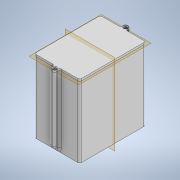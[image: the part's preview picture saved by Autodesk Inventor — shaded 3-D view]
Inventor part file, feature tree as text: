
AUTODESK INVENTOR PART (.ipt)
format: ipt  version: 2020 (Build 240168000, 168)  size: 301,056 bytes
history: native  units: mm
features: sketch x5, extrude x4, plane x2, fillet x2, shell x1, hole x1, chamfer x1, split x1
ambient origin geometry x8: Origin, YZ Plane, XZ Plane, XY Plane, X Axis, Y Axis, Z Axis, Center Point
bodies: Solid1 (feature_tree), Solid4 (feature_tree), Solid5 (feature_tree)
feature tree (17):
  extrude  "Extrusion1"  Depth=42.0mm
  shell  "Shell1"  Thickness=70.0mm
  plane  "Work Plane1"
  extrude  "Extrusion2"  [1 undecoded]
  extrude  "Extrusion3"  Depth=5.0mm
  hole  "Hole1"  [1 undecoded]
  chamfer  "Chamfer1"  Distance=5.0mm
  fillet  "Fillet2"  Radius=2.0mm
  split  "Split2"
  fillet  "Fillet3"  Radius=4.0mm
  plane  "Work Plane2"
  extrude  "Extrusion5"  Depth=2.0mm
  sketch  "Sketch1"  dims[d0=63.0mm d1=42.0mm d2=70.0mm d3=0.0mm]
  sketch  "Sketch3"  dims[d4=2.0mm d5=-2.0mm]
  sketch  "Sketch4"  dims[d9=74.0mm d10=5.0mm]
  sketch  "Sketch6"  dims[d11=5.0mm d12=0.0mm d13=5.0mm d14=5.0mm d15=0.0mm]
  sketch  "Sketch8"  dims[d16=3.242mm d17=8.0mm d18=4.5mm d19=3.4mm d20=90.0deg d21=11.8mm d22=20.594885mm d23=5.0mm d24=2.0mm d25=45.0deg d27=4.0mm d31=2.0mm d32=4.0mm d33=10.0mm d34=10.0mm d35=7.0mm d36=2.0mm d39=3.0mm d40=2.0mm d41=2.0mm d42=2.0mm d43=2.0mm d44=2.0mm d45=20.0mm d46=0.0mm d47=0.5mm d48=0.872665mm d49=0.5mm d50=0.872665mm]
note: 2 required parameter values undecoded (feature->parameter linkage not recoverable at this tier; creation-order binding heuristic only, values carry confidence <= 0.55)
